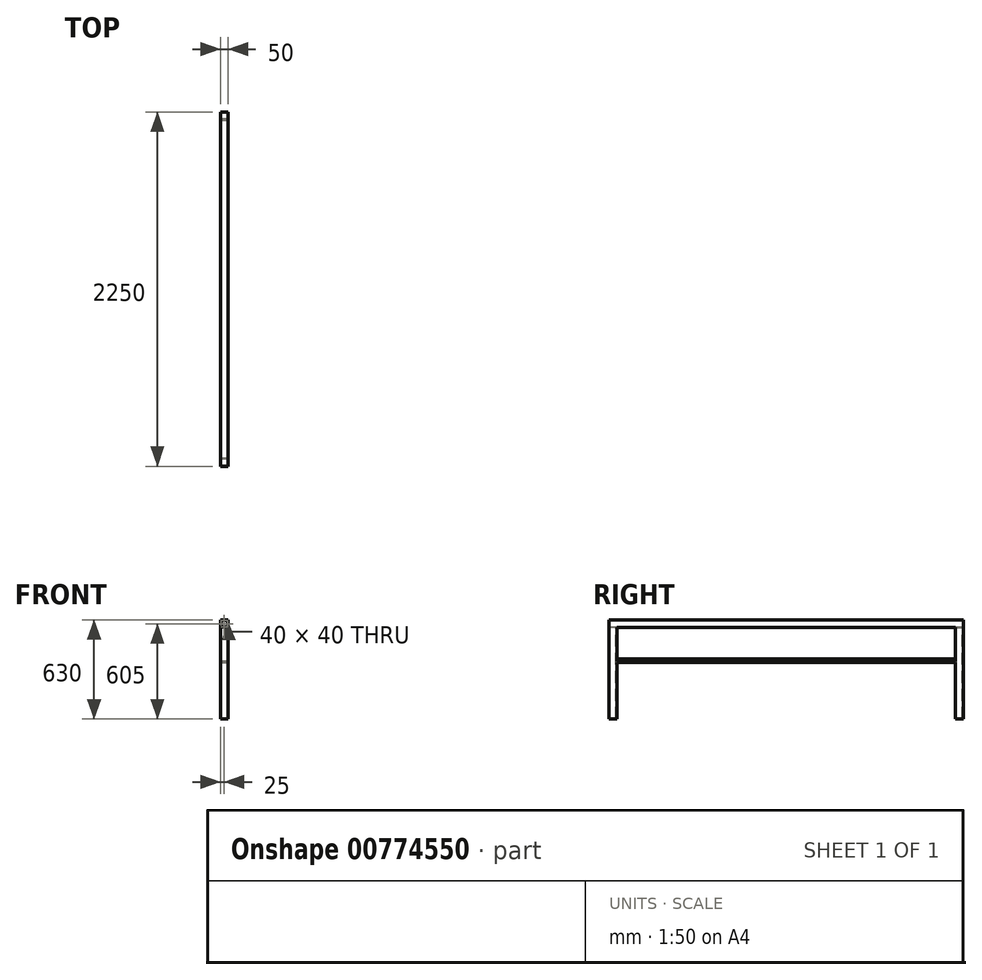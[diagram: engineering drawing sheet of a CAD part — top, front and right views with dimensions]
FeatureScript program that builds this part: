
annotation { "Feature Type Name" : "Feature", "Feature Type Description" : "" }
export const myFeature = defineFeature(function(context is Context, id is Id, definition is map)
    precondition{}
    {
        {
            var Q0;
            Q0=qCreatedBy(makeId("Front.planeOp"),FACE);
            var sketch = newSketch(context, id + "F0", { "sketchPlane" : qUnion([Q0])});
            skLineSegment(sketch, "E0.bottom", {"start": v(25, -25) * mm, "end": v(-25, -25) * mm});
            skLineSegment(sketch, "E0.top", {"start": v(25, 25) * mm, "end": v(-25, 25) * mm});
            skLineSegment(sketch, "E0.left", {"start": v(25, -25) * mm, "end": v(25, 25) * mm});
            skLineSegment(sketch, "E0.right", {"start": v(-25, -25) * mm, "end": v(-25, 25) * mm});
            skPoint(sketch, "E0.middle", {"position": v(0, 0) * mm});
            skLineSegment(sketch, "E1.bottom", {"start": v(20, -20) * mm, "end": v(-20, -20) * mm});
            skLineSegment(sketch, "E1.top", {"start": v(20, 20) * mm, "end": v(-20, 20) * mm});
            skLineSegment(sketch, "E1.left", {"start": v(20, -20) * mm, "end": v(20, 20) * mm});
            skLineSegment(sketch, "E1.right", {"start": v(-20, -20) * mm, "end": v(-20, 20) * mm});
            skSolve(sketch);
        }
        {
            var Q0;
            Q0 = qSketchRegion(id + "F0", true);
            extrude(context, id + "F1", {"entities" : qUnion([Q0]), "depth" : 2250 * mm, "offsetDistance" : 25 * mm});
        }
        {
            var Q0;
            Q0=makeQuery(id+"F1.opExtrude","SWEPT_FACE",FACE,{"disambiguationData":[OSD([sQuery(id+"F0.wireOp",EDGE,"E0.bottom")])]});
            var sketch = newSketch(context, id + "F2", { "sketchPlane" : qUnion([Q0])});
            skLineSegment(sketch, "E2.bottom", {"start": v(-25, 50) * mm, "end": v(25, 50) * mm});
            skLineSegment(sketch, "E2.top", {"start": v(-25, 0) * mm, "end": v(25, 0) * mm});
            skLineSegment(sketch, "E2.left", {"start": v(-25, 50) * mm, "end": v(-25, 0) * mm});
            skLineSegment(sketch, "E2.right", {"start": v(25, 50) * mm, "end": v(25, 0) * mm});
            skLineSegment(sketch, "E3.bottom", {"start": v(20, 45) * mm, "end": v(-20, 45) * mm});
            skLineSegment(sketch, "E3.top", {"start": v(20, 5) * mm, "end": v(-20, 5) * mm});
            skLineSegment(sketch, "E3.left", {"start": v(20, 45) * mm, "end": v(20, 5) * mm});
            skLineSegment(sketch, "E3.right", {"start": v(-20, 45) * mm, "end": v(-20, 5) * mm});
            skLineSegment(sketch, "E4", {"start": v(31.85, 1125) * mm, "end": v(-31.17, 1125) * mm, "construction": true});
            skLineSegment(sketch, "E5.MirrorCS", {"start": v(20, 2245) * mm, "end": v(-20, 2245) * mm});
            skLineSegment(sketch, "E6.MirrorCS", {"start": v(-20, 2205) * mm, "end": v(-20, 2245) * mm});
            skLineSegment(sketch, "E7.MirrorCS", {"start": v(20, 2205) * mm, "end": v(-20, 2205) * mm});
            skLineSegment(sketch, "E8.MirrorCS", {"start": v(-25, 2250) * mm, "end": v(25, 2250) * mm});
            skLineSegment(sketch, "E9.MirrorCS", {"start": v(20, 2205) * mm, "end": v(20, 2245) * mm});
            skLineSegment(sketch, "E10.MirrorCS", {"start": v(-25, 2200) * mm, "end": v(-25, 2250) * mm});
            skLineSegment(sketch, "E11.MirrorCS", {"start": v(-25, 2200) * mm, "end": v(25, 2200) * mm});
            skLineSegment(sketch, "E12.MirrorCS", {"start": v(25, 2200) * mm, "end": v(25, 2250) * mm});
            skSolve(sketch);
        }
        {
            var Q0;
            Q0 = qSketchRegion(id + "F2", true);
            extrude(context, id + "F3", {"entities" : qUnion([Q0]), "operationType" : NewBodyOperationType.ADD, "depth" : 580 * mm, "offsetDistance" : 25 * mm});
        }
        {
            var Q0;
            Q0=makeQuery(id+"F3.opExtrude","SWEPT_FACE",FACE,{"disambiguationData":[OSD([sQuery(id+"F2.wireOp",EDGE,"E2.bottom")])]});
            var sketch = newSketch(context, id + "F4", { "sketchPlane" : qUnion([Q0])});
            skLineSegment(sketch, "E13", {"start": v(-25, -225) * mm, "end": v(-25, -245) * mm});
            skLineSegment(sketch, "E14", {"start": v(-25, -245) * mm, "end": v(25, -245) * mm});
            skLineSegment(sketch, "E15", {"start": v(25, -245) * mm, "end": v(25, -240) * mm});
            skLineSegment(sketch, "E16", {"start": v(25, -240) * mm, "end": v(-20, -240) * mm});
            skLineSegment(sketch, "E17", {"start": v(-20, -240) * mm, "end": v(-20, -225) * mm});
            skLineSegment(sketch, "E18", {"start": v(-25, -225) * mm, "end": v(-20, -225) * mm});
            skSolve(sketch);
        }
        {
            var Q0;
            Q0 = qSketchRegion(id + "F4", true);
            var Q1;
            Q1=makeQuery(id+"F3.opExtrude","SWEPT_FACE",FACE,{"disambiguationData":[OSD([sQuery(id+"F2.wireOp",EDGE,"E11.MirrorCS")])]});
            extrude(context, id + "F5", {"entities" : qUnion([Q0]), "operationType" : NewBodyOperationType.ADD, "endBound" : BoundingType.UP_TO_SURFACE, "depth" : 25 * mm, "endBoundEntityFace" : qUnion([Q1]), "offsetDistance" : 25 * mm});
        }
    });
